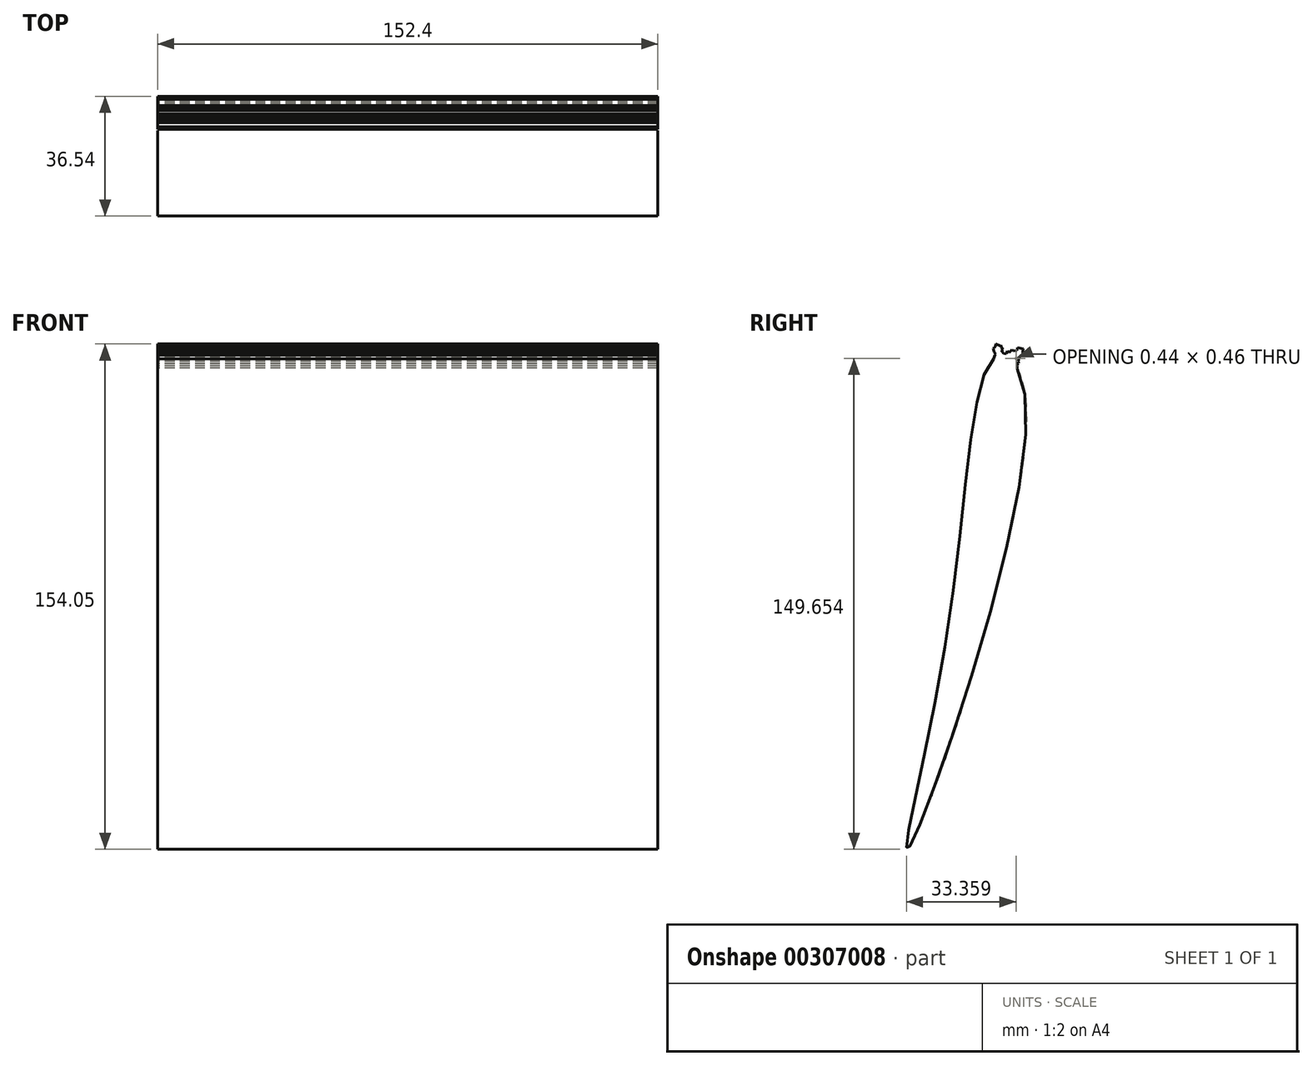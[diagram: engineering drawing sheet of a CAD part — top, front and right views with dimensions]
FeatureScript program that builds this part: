
annotation { "Feature Type Name" : "Feature", "Feature Type Description" : "" }
export const myFeature = defineFeature(function(context is Context, id is Id, definition is map)
    precondition{}
    {
        {
            var Q0;
            Q0=qCreatedBy(makeId("Right.planeOp"),FACE);
            var sketch = newSketch(context, id + "F0", { "sketchPlane" : qUnion([Q0])});
            skFitSpline(sketch, "E0", {"points": [v(24.33, 73.03) * mm, v(33.67, 58.14) * mm, v(-2.03, -76.46) * mm, v(9.72, -9.8) * mm, v(24.33, 73.03) * mm]});
            skLineSegment(sketch, "E1", {"start": v(28.43, 72.69) * mm, "end": v(31.12, 75.12) * mm});
            skLineSegment(sketch, "E2", {"start": v(31.12, 75.12) * mm, "end": v(32.05, 74.22) * mm});
            skLineSegment(sketch, "E3", {"start": v(32.05, 74.22) * mm, "end": v(29.56, 71.64) * mm});
            skLineSegment(sketch, "E4", {"start": v(29.56, 71.64) * mm, "end": v(28.43, 72.69) * mm});
            skLineSegment(sketch, "E5", {"start": v(31.12, 75.12) * mm, "end": v(31.78, 75.8) * mm});
            skPoint(sketch, "E5.endSnap0", {"position": v(31.58, 74.67) * mm});
            skLineSegment(sketch, "E6", {"start": v(31.78, 75.8) * mm, "end": v(32.65, 74.85) * mm});
            skLineSegment(sketch, "E7", {"start": v(32.65, 74.85) * mm, "end": v(32.05, 74.22) * mm});
            skLineSegment(sketch, "E8", {"start": v(26.06, 73.54) * mm, "end": v(25.48, 76.11) * mm});
            skLineSegment(sketch, "E9", {"start": v(25.48, 76.11) * mm, "end": v(24.2, 75.82) * mm});
            skLineSegment(sketch, "E10", {"start": v(24.2, 75.82) * mm, "end": v(24.79, 73.27) * mm});
            skLineSegment(sketch, "E11", {"start": v(24.79, 73.27) * mm, "end": v(26.06, 73.54) * mm});
            skLineSegment(sketch, "E12", {"start": v(30.11, 71.07) * mm, "end": v(30.36, 72.48) * mm});
            skLineSegment(sketch, "E13", {"start": v(30.36, 72.48) * mm, "end": v(30.8, 72.93) * mm});
            skLineSegment(sketch, "E14", {"start": v(30.8, 72.93) * mm, "end": v(30.75, 72.67) * mm});
            skPoint(sketch, "E14.endSnap0", {"position": v(30.58, 72.7) * mm});
            skLineSegment(sketch, "E15", {"start": v(30.75, 72.67) * mm, "end": v(30.36, 72.48) * mm});
            skLineSegment(sketch, "E16", {"start": v(30.23, 71.77) * mm, "end": v(30.94, 72.5) * mm});
            skLineSegment(sketch, "E17", {"start": v(30.94, 72.5) * mm, "end": v(31.07, 73.21) * mm});
            skLineSegment(sketch, "E18", {"start": v(31.07, 73.21) * mm, "end": v(31.48, 72.82) * mm});
            skLineSegment(sketch, "E19", {"start": v(31.48, 72.82) * mm, "end": v(30.94, 72.5) * mm});
            skLineSegment(sketch, "E20", {"start": v(31.7, 73.86) * mm, "end": v(32.53, 73.72) * mm});
            skLineSegment(sketch, "E21", {"start": v(32.53, 73.72) * mm, "end": v(32.05, 74.22) * mm});
            skLineSegment(sketch, "E22", {"start": v(32.65, 74.85) * mm, "end": v(32.6, 74.12) * mm});
            skLineSegment(sketch, "E23", {"start": v(32.6, 74.12) * mm, "end": v(31.9, 73.39) * mm});
            skLineSegment(sketch, "E24", {"start": v(31.9, 73.39) * mm, "end": v(31.07, 73.21) * mm});
            skLineSegment(sketch, "E25", {"start": v(31.9, 73.39) * mm, "end": v(31.84, 73.07) * mm});
            skLineSegment(sketch, "E26", {"start": v(31.84, 73.07) * mm, "end": v(31.48, 72.82) * mm});
            skLineSegment(sketch, "E27", {"start": v(32.6, 74.12) * mm, "end": v(32.05, 74.22) * mm});
            skLineSegment(sketch, "E28", {"start": v(31.48, 72.82) * mm, "end": v(31.3, 71.86) * mm});
            skLineSegment(sketch, "E29", {"start": v(31.3, 71.86) * mm, "end": v(30.23, 71.77) * mm});
            skLineSegment(sketch, "E30", {"start": v(32.65, 74.85) * mm, "end": v(32.8, 75.63) * mm});
            skLineSegment(sketch, "E31", {"start": v(32.8, 75.63) * mm, "end": v(32.35, 75.18) * mm});
            skLineSegment(sketch, "E32", {"start": v(32.35, 75.18) * mm, "end": v(32.8, 75.63) * mm});
            skLineSegment(sketch, "E33", {"start": v(32.8, 75.63) * mm, "end": v(31.78, 75.8) * mm});
            skLineSegment(sketch, "E34", {"start": v(31.78, 75.8) * mm, "end": v(30.97, 75.95) * mm});
            skLineSegment(sketch, "E35", {"start": v(30.97, 75.95) * mm, "end": v(30.83, 75.17) * mm});
            skLineSegment(sketch, "E36", {"start": v(30.83, 75.17) * mm, "end": v(29.84, 74.98) * mm});
            skLineSegment(sketch, "E37", {"start": v(29.84, 74.98) * mm, "end": v(29.38, 75.43) * mm});
            skLineSegment(sketch, "E38", {"start": v(29.38, 75.43) * mm, "end": v(29.18, 74.3) * mm});
            skLineSegment(sketch, "E39", {"start": v(29.18, 74.3) * mm, "end": v(29.1, 73.88) * mm});
            skLineSegment(sketch, "E40", {"start": v(29.1, 73.88) * mm, "end": v(28.37, 73.83) * mm});
            skLineSegment(sketch, "E41", {"start": v(28.37, 73.83) * mm, "end": v(28.21, 72.95) * mm});
            skLineSegment(sketch, "E42", {"start": v(28.21, 72.95) * mm, "end": v(28.43, 72.69) * mm});
            skLineSegment(sketch, "E43", {"start": v(29.38, 75.43) * mm, "end": v(28.43, 74.44) * mm});
            skLineSegment(sketch, "E44", {"start": v(28.43, 74.44) * mm, "end": v(27.9, 74.95) * mm});
            skLineSegment(sketch, "E45", {"start": v(27.9, 74.95) * mm, "end": v(27.52, 74.16) * mm});
            skLineSegment(sketch, "E46", {"start": v(27.52, 74.16) * mm, "end": v(26.8, 74.29) * mm});
            skLineSegment(sketch, "E47", {"start": v(26.8, 74.29) * mm, "end": v(26.25, 73.7) * mm});
            skLineSegment(sketch, "E48", {"start": v(26.8, 74.29) * mm, "end": v(26.25, 74.82) * mm});
            skLineSegment(sketch, "E49", {"start": v(26.25, 74.82) * mm, "end": v(25.89, 74.45) * mm});
            skLineSegment(sketch, "E50", {"start": v(25.89, 74.45) * mm, "end": v(26.04, 75.28) * mm});
            skLineSegment(sketch, "E51", {"start": v(26.04, 75.28) * mm, "end": v(25.57, 75.73) * mm});
            skLineSegment(sketch, "E52", {"start": v(25.57, 75.73) * mm, "end": v(25.48, 76.11) * mm});
            skLineSegment(sketch, "E53", {"start": v(26.04, 75.28) * mm, "end": v(26.16, 76) * mm});
            skLineSegment(sketch, "E54", {"start": v(26.16, 76) * mm, "end": v(25.57, 75.73) * mm});
            skLineSegment(sketch, "E55", {"start": v(26.16, 76) * mm, "end": v(26.63, 75.54) * mm});
            skLineSegment(sketch, "E56", {"start": v(26.63, 75.54) * mm, "end": v(26.04, 75.28) * mm});
            skLineSegment(sketch, "E57", {"start": v(26.16, 76) * mm, "end": v(25.97, 76.83) * mm});
            skLineSegment(sketch, "E58", {"start": v(25.97, 76.83) * mm, "end": v(25.48, 76.11) * mm});
            skLineSegment(sketch, "E59", {"start": v(25.48, 76.11) * mm, "end": v(24.96, 76.62) * mm});
            skPoint(sketch, "E59.endSnap0", {"position": v(24.84, 75.97) * mm});
            skLineSegment(sketch, "E60", {"start": v(24.96, 76.62) * mm, "end": v(24.2, 75.82) * mm});
            skLineSegment(sketch, "E61", {"start": v(24.2, 75.82) * mm, "end": v(24.43, 77.1) * mm});
            skLineSegment(sketch, "E62", {"start": v(24.43, 77.1) * mm, "end": v(25.72, 76.47) * mm});
            skLineSegment(sketch, "E63", {"start": v(25.72, 76.47) * mm, "end": v(25.97, 76.83) * mm});
            skLineSegment(sketch, "E64", {"start": v(24.3, 76.32) * mm, "end": v(23.69, 75.7) * mm});
            skLineSegment(sketch, "E65", {"start": v(23.69, 75.7) * mm, "end": v(24.56, 74.36) * mm});
            skLineSegment(sketch, "E66", {"start": v(24.56, 74.36) * mm, "end": v(23.92, 74.8) * mm});
            skLineSegment(sketch, "E67", {"start": v(23.92, 74.8) * mm, "end": v(23.82, 75.25) * mm});
            skLineSegment(sketch, "E68", {"start": v(23.82, 75.25) * mm, "end": v(23.69, 75.7) * mm});
            skLineSegment(sketch, "E69", {"start": v(24.79, 73.27) * mm, "end": v(24.33, 73.03) * mm});
            skLineSegment(sketch, "E70", {"start": v(24.33, 73.03) * mm, "end": v(24.17, 73.7) * mm});
            skLineSegment(sketch, "E71", {"start": v(24.17, 73.7) * mm, "end": v(24.62, 74.26) * mm});
            skLineSegment(sketch, "E72", {"start": v(24.62, 74.26) * mm, "end": v(23.92, 74.8) * mm});
            skLineSegment(sketch, "E73", {"start": v(23.92, 74.8) * mm, "end": v(24.4, 73.98) * mm});
            skLineSegment(sketch, "E74", {"start": v(31.3, 71.86) * mm, "end": v(31.36, 71.16) * mm});
            skLineSegment(sketch, "E75", {"start": v(31.36, 71.16) * mm, "end": v(30.84, 71.06) * mm});
            skLineSegment(sketch, "E76", {"start": v(30.84, 71.06) * mm, "end": v(30.96, 70.44) * mm});
            skLineSegment(sketch, "E77", {"start": v(30.96, 70.44) * mm, "end": v(30.85, 69.78) * mm});
            skLineSegment(sketch, "E78", {"start": v(30.85, 69.78) * mm, "end": v(30.11, 71.07) * mm});
            skLineSegment(sketch, "E79", {"start": v(24.17, 73.7) * mm, "end": v(23.74, 72.6) * mm});
            skLineSegment(sketch, "E80", {"start": v(23.74, 72.6) * mm, "end": v(24.33, 73.03) * mm});
            skLineSegment(sketch, "E81", {"start": v(26.04, 75.28) * mm, "end": v(26.25, 74.82) * mm});
            skLineSegment(sketch, "E82.0", {"start": v(24.17, 73.7) * mm, "end": v(30.94, 72.5) * mm, "construction": true});
            skLineSegment(sketch, "E83.0", {"start": v(23.82, 75.25) * mm, "end": v(32.53, 73.72) * mm, "construction": true});
            skLineSegment(sketch, "E84.0", {"start": v(23.92, 74.8) * mm, "end": v(26.8, 74.29) * mm, "construction": true});
            skLineSegment(sketch, "E85.0", {"start": v(24.56, 74.36) * mm, "end": v(31.84, 73.07) * mm, "construction": true});
            skLineSegment(sketch, "E86.0", {"start": v(23.69, 75.7) * mm, "end": v(32.6, 74.12) * mm, "construction": true});
            skLineSegment(sketch, "E87.0", {"start": v(24.43, 77.1) * mm, "end": v(32.8, 75.63) * mm, "construction": true});
            skLineSegment(sketch, "E88.0", {"start": v(24.3, 76.32) * mm, "end": v(32.65, 74.85) * mm, "construction": true});
            skLineSegment(sketch, "E89.0", {"start": v(25.57, 75.73) * mm, "end": v(31.58, 74.67) * mm, "construction": true});
            skLineSegment(sketch, "E90.0", {"start": v(30.58, 72.7) * mm, "end": v(30.75, 72.67) * mm, "construction": true});
            skLineSegment(sketch, "E91.0", {"start": v(28.43, 74.44) * mm, "end": v(29.18, 74.3) * mm, "construction": true});
            skLineSegment(sketch, "E92.0", {"start": v(29.1, 73.88) * mm, "end": v(31.9, 73.39) * mm, "construction": true});
            skLineSegment(sketch, "E93.0", {"start": v(24.56, 74.36) * mm, "end": v(24.96, 76.62) * mm, "construction": true});
            skLineSegment(sketch, "E94.0", {"start": v(31.9, 73.39) * mm, "end": v(32.05, 74.22) * mm, "construction": true});
            skLineSegment(sketch, "E95.0", {"start": v(24.2, 75.82) * mm, "end": v(24.3, 76.32) * mm, "construction": true});
            skLineSegment(sketch, "E96.0", {"start": v(31.58, 74.67) * mm, "end": v(31.78, 75.8) * mm, "construction": true});
            skLineSegment(sketch, "E97.0", {"start": v(30.23, 71.77) * mm, "end": v(30.97, 75.95) * mm, "construction": true});
            skLineSegment(sketch, "E98.0", {"start": v(32.53, 73.72) * mm, "end": v(32.6, 74.12) * mm, "construction": true});
            skSolve(sketch);
        }
        {
            var Q0;
            Q0=qSketchRegion(id+"F0",true);
            var Q1;
            Q1=makeQuery(id+"F0.imprint","IMPRINT",FACE,{"disambiguationData":[TD([[makeQuery(id+"F0.imprint","IMPRINT",EDGE,{"derivedFrom":sQuery(id+"F0.wireOp",EDGE,"E1")}),1.0]])]});
            var Q2;
            {var subQ3=sQuery(id+"F0.wireOp",EDGE,"E1");Q2=makeQuery(id+"F0.imprint","IMPRINT",FACE,{"disambiguationData":[TD([[makeQuery(id+"F0.imprint","IMPRINT",EDGE,{"derivedFrom":subQ3}),-1.0]])]});}
            var Q3;
            {var subQ0=sQuery(id+"F0.wireOp",EDGE,"E29");Q3=makeQuery(id+"F0.imprint","IMPRINT",FACE,{"disambiguationData":[TD([[makeQuery(id+"F0.imprint","IMPRINT",EDGE,{"derivedFrom":subQ0}),1.0]])]});}
            var Q4;
            {var subQ0=sQuery(id+"F0.wireOp",EDGE,"E78");var subQ1=sQuery(id+"F0.wireOp",EDGE,"E12");var subQ2=makeQuery(id+"F0.imprint","INTERSECT",VERTEX,{"derivedFrom":[subQ1,subQ0]});Q4=makeQuery(id+"F0.imprint","IMPRINT",FACE,{"disambiguationData":[TD([[makeQuery(id+"F0.imprint","IMPRINT",EDGE,{"disambiguationData":[TD([[subQ2,1.0]])],"derivedFrom":subQ0}),1.0]])]});}
            var Q5;
            {var subQ2=sQuery(id+"F0.wireOp",EDGE,"E8");Q5=makeQuery(id+"F0.imprint","IMPRINT",FACE,{"disambiguationData":[TD([[makeQuery(id+"F0.imprint","IMPRINT",EDGE,{"derivedFrom":subQ2}),-1.0]])]});}
            var Q6;
            {var subQ0=sQuery(id+"F0.wireOp",EDGE,"E11");Q6=makeQuery(id+"F0.imprint","IMPRINT",FACE,{"disambiguationData":[TD([[makeQuery(id+"F0.imprint","IMPRINT",EDGE,{"derivedFrom":subQ0}),1.0]])]});}
            var Q7;
            {var subQ0=sQuery(id+"F0.wireOp",EDGE,"E4");Q7=makeQuery(id+"F0.imprint","IMPRINT",FACE,{"disambiguationData":[TD([[makeQuery(id+"F0.imprint","IMPRINT",EDGE,{"derivedFrom":subQ0}),-1.0]])]});}
            var Q8;
            {var subQ0=sQuery(id+"F0.wireOp",EDGE,"E78");var subQ1=sQuery(id+"F0.wireOp",EDGE,"E0");var subQ3=makeQuery(id+"F0.imprint","INTERSECT",VERTEX,{"derivedFrom":[subQ1,subQ0]});Q8=makeQuery(id+"F0.imprint","IMPRINT",FACE,{"disambiguationData":[TD([[makeQuery(id+"F0.imprint","IMPRINT",EDGE,{"disambiguationData":[TD([[subQ3,-1.0]])],"derivedFrom":subQ1}),-1.0]])]});}
            var Q9;
            {var subQ6=sQuery(id+"F0.wireOp",EDGE,"E8");Q9=makeQuery(id+"F0.imprint","IMPRINT",FACE,{"disambiguationData":[TD([[makeQuery(id+"F0.imprint","IMPRINT",EDGE,{"derivedFrom":subQ6}),1.0]])]});}
            var Q10;
            Q10=makeQuery(id+"F0.imprint","IMPRINT",FACE,{"disambiguationData":[TD([[makeQuery(id+"F0.imprint","IMPRINT",EDGE,{"derivedFrom":sQuery(id+"F0.wireOp",EDGE,"E58")}),-1.0]])]});
            var Q11;
            {var subQ0=sQuery(id+"F0.wireOp",EDGE,"E69");Q11=makeQuery(id+"F0.imprint","IMPRINT",FACE,{"disambiguationData":[TD([[makeQuery(id+"F0.imprint","IMPRINT",EDGE,{"derivedFrom":subQ0}),-1.0]])]});}
            var Q12;
            {var subQ1=sQuery(id+"F0.wireOp",EDGE,"E70");Q12=makeQuery(id+"F0.imprint","IMPRINT",FACE,{"disambiguationData":[TD([[makeQuery(id+"F0.imprint","IMPRINT",EDGE,{"derivedFrom":subQ1}),1.0]])]});}
            var Q13;
            {var subQ0=sQuery(id+"F0.wireOp",EDGE,"E80");Q13=makeQuery(id+"F0.imprint","IMPRINT",FACE,{"disambiguationData":[TD([[makeQuery(id+"F0.imprint","IMPRINT",EDGE,{"derivedFrom":subQ0}),1.0]])]});}
            var Q14;
            {var subQ5=sQuery(id+"F0.wireOp",EDGE,"E64");Q14=makeQuery(id+"F0.imprint","IMPRINT",FACE,{"disambiguationData":[TD([[makeQuery(id+"F0.imprint","IMPRINT",EDGE,{"derivedFrom":subQ5}),1.0]])]});}
            var Q15;
            {var subQ1=sQuery(id+"F0.wireOp",EDGE,"E70");Q15=makeQuery(id+"F0.imprint","IMPRINT",FACE,{"disambiguationData":[TD([[makeQuery(id+"F0.imprint","IMPRINT",EDGE,{"derivedFrom":subQ1}),-1.0]])]});}
            var Q16;
            {var subQ0=sQuery(id+"F0.wireOp",EDGE,"E67");Q16=makeQuery(id+"F0.imprint","IMPRINT",FACE,{"disambiguationData":[TD([[makeQuery(id+"F0.imprint","IMPRINT",EDGE,{"derivedFrom":subQ0}),-1.0]])]});}
            var Q17;
            {var subQ0=sQuery(id+"F0.wireOp",EDGE,"E72");var subQ1=sQuery(id+"F0.wireOp",EDGE,"E10");var subQ2=makeQuery(id+"F0.imprint","INTERSECT",VERTEX,{"derivedFrom":[subQ1,subQ0]});Q17=makeQuery(id+"F0.imprint","IMPRINT",FACE,{"disambiguationData":[TD([[makeQuery(id+"F0.imprint","IMPRINT",EDGE,{"disambiguationData":[TD([[subQ2,-1.0]])],"derivedFrom":subQ1}),1.0]])]});}
            var Q18;
            Q18=makeQuery(id+"F0.imprint","IMPRINT",FACE,{"disambiguationData":[TD([[makeQuery(id+"F0.imprint","IMPRINT",EDGE,{"derivedFrom":sQuery(id+"F0.wireOp",EDGE,"E9")}),-1.0]])]});
            var Q19;
            Q19=makeQuery(id+"F0.imprint","IMPRINT",FACE,{"disambiguationData":[TD([[makeQuery(id+"F0.imprint","IMPRINT",EDGE,{"derivedFrom":sQuery(id+"F0.wireOp",EDGE,"E17")}),-1.0]])]});
            var Q20;
            {var subQ0=sQuery(id+"F0.wireOp",EDGE,"E65");var subQ1=sQuery(id+"F0.wireOp",EDGE,"E10");var subQ2=makeQuery(id+"F0.imprint","INTERSECT",VERTEX,{"derivedFrom":[subQ1,subQ0]});Q20=makeQuery(id+"F0.imprint","IMPRINT",FACE,{"disambiguationData":[TD([[makeQuery(id+"F0.imprint","IMPRINT",EDGE,{"disambiguationData":[TD([[subQ2,-1.0]])],"derivedFrom":subQ1}),1.0]])]});}
            var Q21;
            Q21=makeQuery(id+"F0.imprint","IMPRINT",FACE,{"disambiguationData":[TD([[makeQuery(id+"F0.imprint","IMPRINT",EDGE,{"derivedFrom":sQuery(id+"F0.wireOp",EDGE,"E18")}),1.0]])]});
            var Q22;
            Q22=makeQuery(id+"F0.imprint","IMPRINT",FACE,{"disambiguationData":[TD([[makeQuery(id+"F0.imprint","IMPRINT",EDGE,{"derivedFrom":sQuery(id+"F0.wireOp",EDGE,"E49")}),-1.0]])]});
            var Q23;
            {var subQ2=sQuery(id+"F0.wireOp",EDGE,"E32");Q23=makeQuery(id+"F0.imprint","IMPRINT",FACE,{"disambiguationData":[TD([[makeQuery(id+"F0.imprint","IMPRINT",EDGE,{"derivedFrom":subQ2}),1.0]])]});}
            var Q24;
            {var subQ0=sQuery(id+"F0.wireOp",EDGE,"E66");var subQ1=sQuery(id+"F0.wireOp",EDGE,"E10");var subQ2=makeQuery(id+"F0.imprint","INTERSECT",VERTEX,{"derivedFrom":[subQ1,subQ0]});Q24=makeQuery(id+"F0.imprint","IMPRINT",FACE,{"disambiguationData":[TD([[makeQuery(id+"F0.imprint","IMPRINT",EDGE,{"disambiguationData":[TD([[subQ2,-1.0]])],"derivedFrom":subQ1}),-1.0]])]});}
            var Q25;
            Q25=makeQuery(id+"F0.imprint","IMPRINT",FACE,{"disambiguationData":[TD([[makeQuery(id+"F0.imprint","IMPRINT",EDGE,{"derivedFrom":sQuery(id+"F0.wireOp",EDGE,"E2")}),1.0]])]});
            var Q26;
            {var subQ5=sQuery(id+"F0.wireOp",EDGE,"E73");Q26=makeQuery(id+"F0.imprint","IMPRINT",FACE,{"disambiguationData":[TD([[makeQuery(id+"F0.imprint","IMPRINT",EDGE,{"derivedFrom":subQ5}),1.0]])]});}
            var Q27;
            {var subQ1=sQuery(id+"F0.wireOp",EDGE,"E14");Q27=makeQuery(id+"F0.imprint","IMPRINT",FACE,{"disambiguationData":[TD([[makeQuery(id+"F0.imprint","IMPRINT",EDGE,{"derivedFrom":subQ1}),1.0]])]});}
            var Q28;
            Q28=makeQuery(id+"F0.imprint","IMPRINT",FACE,{"disambiguationData":[TD([[makeQuery(id+"F0.imprint","IMPRINT",EDGE,{"derivedFrom":sQuery(id+"F0.wireOp",EDGE,"E16")}),-1.0]])]});
            var Q29;
            {var subQ0=sQuery(id+"F0.wireOp",EDGE,"E24");Q29=makeQuery(id+"F0.imprint","IMPRINT",FACE,{"disambiguationData":[TD([[makeQuery(id+"F0.imprint","IMPRINT",EDGE,{"derivedFrom":subQ0}),-1.0]])]});}
            var Q30;
            Q30=makeQuery(id+"F0.imprint","IMPRINT",FACE,{"disambiguationData":[TD([[makeQuery(id+"F0.imprint","IMPRINT",EDGE,{"derivedFrom":sQuery(id+"F0.wireOp",EDGE,"E13")}),-1.0]])]});
            var Q31;
            {var subQ0=sQuery(id+"F0.wireOp",EDGE,"E21");var subQ1=sQuery(id+"F0.wireOp",EDGE,"E20");var subQ2=makeQuery(id+"F0.imprint","INTERSECT",VERTEX,{"derivedFrom":[subQ1,subQ0]});Q31=makeQuery(id+"F0.imprint","IMPRINT",FACE,{"disambiguationData":[TD([[makeQuery(id+"F0.imprint","IMPRINT",EDGE,{"disambiguationData":[TD([[subQ2,1.0]])],"derivedFrom":subQ1}),1.0]])]});}
            var Q32;
            Q32=makeQuery(id+"F0.imprint","IMPRINT",FACE,{"disambiguationData":[TD([[makeQuery(id+"F0.imprint","IMPRINT",EDGE,{"derivedFrom":sQuery(id+"F0.wireOp",EDGE,"E53")}),-1.0]])]});
            var Q33;
            {var subQ0=sQuery(id+"F0.wireOp",EDGE,"E30");Q33=makeQuery(id+"F0.imprint","IMPRINT",FACE,{"disambiguationData":[TD([[makeQuery(id+"F0.imprint","IMPRINT",EDGE,{"derivedFrom":subQ0}),1.0]])]});}
            var Q34;
            Q34=makeQuery(id+"F0.imprint","IMPRINT",FACE,{"disambiguationData":[TD([[makeQuery(id+"F0.imprint","IMPRINT",EDGE,{"derivedFrom":sQuery(id+"F0.wireOp",EDGE,"E7")}),1.0]])]});
            var Q35;
            Q35=makeQuery(id+"F0.imprint","IMPRINT",FACE,{"disambiguationData":[TD([[makeQuery(id+"F0.imprint","IMPRINT",EDGE,{"derivedFrom":sQuery(id+"F0.wireOp",EDGE,"E51")}),-1.0]])]});
            var Q36;
            Q36=makeQuery(id+"F0.imprint","IMPRINT",FACE,{"disambiguationData":[TD([[makeQuery(id+"F0.imprint","IMPRINT",EDGE,{"derivedFrom":sQuery(id+"F0.wireOp",EDGE,"E52")}),-1.0]])]});
            var Q37;
            {var subQ1=sQuery(id+"F0.wireOp",EDGE,"E3");var subQ3=sQuery(id+"F0.wireOp",EDGE,"E20");var subQ4=makeQuery(id+"F0.imprint","INTERSECT",VERTEX,{"derivedFrom":[subQ1,subQ3]});Q37=makeQuery(id+"F0.imprint","IMPRINT",FACE,{"disambiguationData":[TD([[makeQuery(id+"F0.imprint","IMPRINT",EDGE,{"disambiguationData":[TD([[subQ4,-1.0]])],"derivedFrom":subQ3}),1.0]])]});}
            var Q38;
            {var subQ0=sQuery(id+"F0.wireOp",EDGE,"E27");Q38=makeQuery(id+"F0.imprint","IMPRINT",FACE,{"disambiguationData":[TD([[makeQuery(id+"F0.imprint","IMPRINT",EDGE,{"derivedFrom":subQ0}),1.0]])]});}
            var Q39;
            {var subQ4=sQuery(id+"F0.wireOp",EDGE,"E4");Q39=makeQuery(id+"F0.imprint","IMPRINT",FACE,{"disambiguationData":[TD([[makeQuery(id+"F0.imprint","IMPRINT",EDGE,{"derivedFrom":subQ4}),1.0]])]});}
            extrude(context, id + "F1", {"entities" : qUnion([Q0, Q1, Q2, Q3, Q4, Q5, Q6, Q7, Q8, Q9, Q10, Q11, Q12, Q13, Q14, Q15, Q16, Q17, Q18, Q19, Q20, Q21, Q22, Q23, Q24, Q25, Q26, Q27, Q28, Q29, Q30, Q31, Q32, Q33, Q34, Q35, Q36, Q37, Q38, Q39]), "depth" : 76.2 * mm, "hasSecondDirection" : true, "secondDirectionOppositeDirection" : true, "secondDirectionDepth" : 76.2 * mm});
        }
    });
